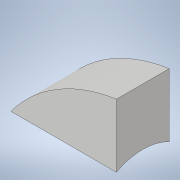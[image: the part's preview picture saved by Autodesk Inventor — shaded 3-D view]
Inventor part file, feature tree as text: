
AUTODESK INVENTOR PART (.ipt)
format: ipt  version: 2020.3 (Build 243373000, 373)  size: 104,448 bytes
history: native  units: mm
features: extrude x2, sketch x2
ambient origin geometry x8: Origin, YZ Plane, XZ Plane, XY Plane, X Axis, Y Axis, Z Axis, Center Point
bodies: Solid1 (feature_tree)
feature tree (4):
  extrude  "Extrusion1"  Depth=30.0mm
  extrude  "Extrusion2"  Depth=26.8mm
  sketch  "Sketch1"  dims[d0=53.6mm d3=30.0mm]
  sketch  "Sketch2"  dims[d4=25.0mm d5=26.8mm d6=50.0mm d7=0.0mm d8=25.0mm d9=0.0mm]
